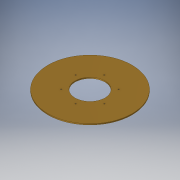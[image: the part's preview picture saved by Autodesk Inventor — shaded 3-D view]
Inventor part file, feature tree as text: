
AUTODESK INVENTOR PART (.ipt)
format: ipt  version: 2018 (Build 220112000, 112)  size: 116,224 bytes
history: native  units: in
note: dims shown in document units (in); Inventor stores cm internally (conversion verified against a paired STEP export)
features: sketch x2, extrude x1, hole x1, pattern_circular x1
ambient origin geometry x8: Origin, YZ Plane, XZ Plane, XY Plane, X Axis, Y Axis, Z Axis, Center Point
bodies: Solid1 (feature_tree)
feature tree (5):
  extrude  "Extrusion1"  Depth=2.5in
  hole  "Hole1"  [1 undecoded]
  pattern_circular  "Circular Pattern1"  Angle=45.0deg  [1 undecoded]
  sketch  "Sketch1"  dims[d0=7.75in d1=2.5in]
  sketch  "Sketch2"  dims[d2=0.1in d3=0.0in d4=1.875in d5=45.0deg d6=0.112in d7=0.276in d8=0.375in d9=0.25in d10=0.5635in d11=0.41in d12=0.8108in d13=2.3622in d14=360.0deg]
note: 2 required parameter values undecoded (feature->parameter linkage not recoverable at this tier; creation-order binding heuristic only, values carry confidence <= 0.55)
